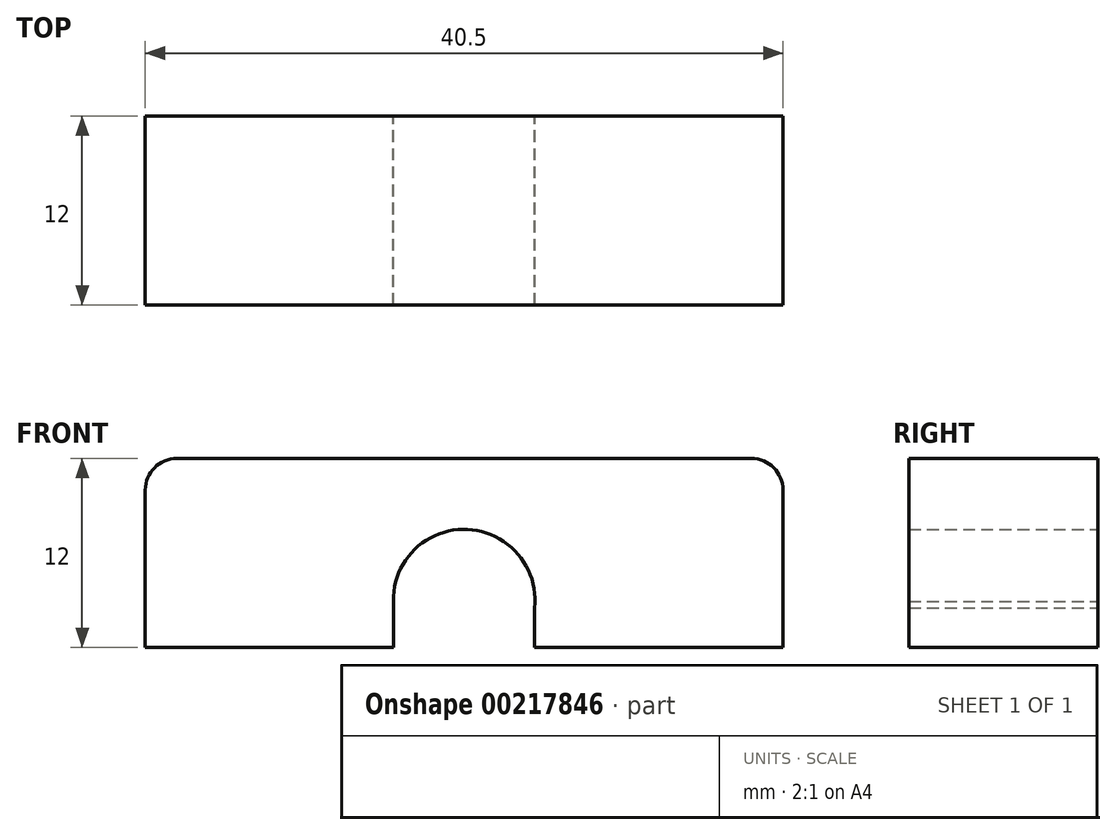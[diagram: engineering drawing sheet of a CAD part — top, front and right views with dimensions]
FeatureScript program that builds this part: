
annotation { "Feature Type Name" : "Feature", "Feature Type Description" : "" }
export const myFeature = defineFeature(function(context is Context, id is Id, definition is map)
    precondition{}
    {
        {
            var Q0;
            Q0=qCreatedBy(makeId("Front.planeOp"),FACE);
            var sketch = newSketch(context, id + "F0", { "sketchPlane" : qUnion([Q0])});
            skLineSegment(sketch, "E0.bottom", {"start": v(-20.25, 6) * mm, "end": v(20.25, 6) * mm});
            skLineSegment(sketch, "E0.top", {"start": v(-20.25, -6) * mm, "end": v(20.25, -6) * mm});
            skLineSegment(sketch, "E0.left", {"start": v(-20.25, 6) * mm, "end": v(-20.25, -6) * mm});
            skLineSegment(sketch, "E0.right", {"start": v(20.25, 6) * mm, "end": v(20.25, -6) * mm});
            skPoint(sketch, "E0.middle", {"position": v(0, 0) * mm});
            skCircle(sketch, "E1", {"center": v(0, -3) * mm, "radius": 4.5 * mm});
            skLineSegment(sketch, "E2.bottom", {"start": v(-4.5, -3.06) * mm, "end": v(4.47, -3.06) * mm});
            skLineSegment(sketch, "E2.top", {"start": v(-4.5, -9.74) * mm, "end": v(4.47, -9.74) * mm});
            skLineSegment(sketch, "E2.left", {"start": v(-4.5, -3.06) * mm, "end": v(-4.5, -9.74) * mm});
            skLineSegment(sketch, "E2.right", {"start": v(4.47, -3.06) * mm, "end": v(4.47, -9.74) * mm});
            skSolve(sketch);
        }
        {
            var Q0;
            Q0=makeQuery(id+"F0.imprint","IMPRINT",FACE,{"disambiguationData":[TD([[makeQuery(id+"F0.imprint","IMPRINT",EDGE,{"derivedFrom":sQuery(id+"F0.wireOp",EDGE,"E0.bottom")}),-1.0]])]});
            extrude(context, id + "F1", {"entities" : qUnion([Q0]), "depth" : 12 * mm});
        }
        {
            var Q0;
            Q0=makeQuery(id+"F1.opExtrude","SWEPT_EDGE",EDGE,{"disambiguationData":[OSD([sQuery(id+"F0.wireOp",EDGE,"E0.bottom"),sQuery(id+"F0.wireOp",EDGE,"E0.right")])]});
            var Q1;
            Q1=makeQuery(id+"F1.opExtrude","SWEPT_EDGE",EDGE,{"disambiguationData":[OSD([sQuery(id+"F0.wireOp",EDGE,"E0.bottom"),sQuery(id+"F0.wireOp",EDGE,"E0.left")])]});
            fillet(context, id + "F2", {"entities" : qUnion([Q0, Q1]), "radius" : 2 * mm, "tangentPropagation" : true, "allowEdgeOverflow" : false});
        }
    });
